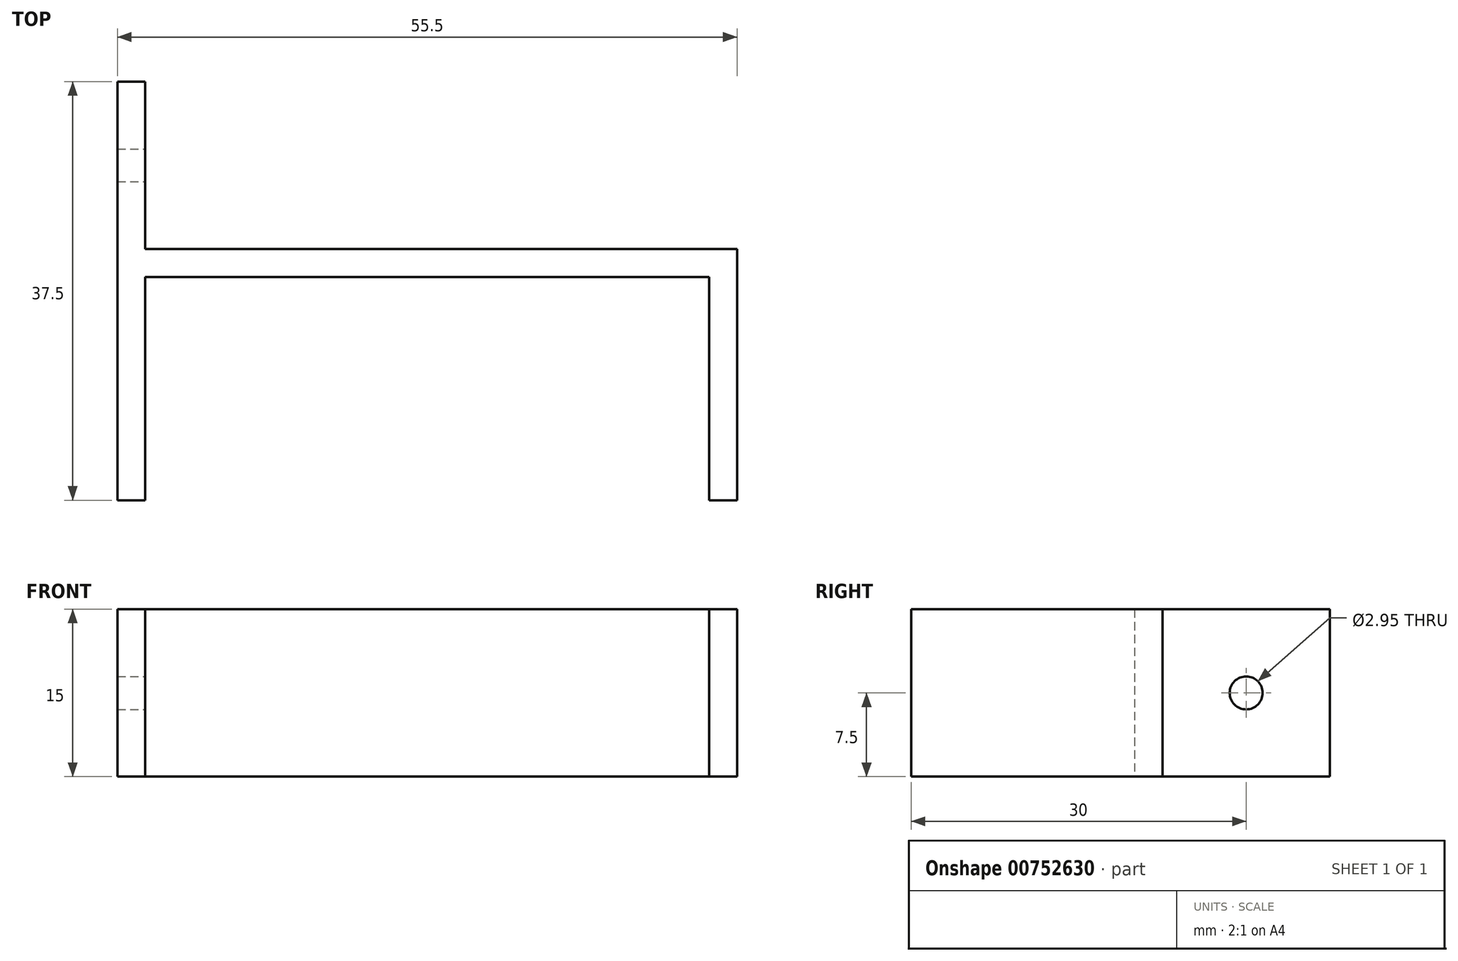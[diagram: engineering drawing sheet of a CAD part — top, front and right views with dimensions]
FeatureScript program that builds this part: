
annotation { "Feature Type Name" : "Feature", "Feature Type Description" : "" }
export const myFeature = defineFeature(function(context is Context, id is Id, definition is map)
    precondition{}
    {
        {
            var Q0;
            Q0=qCreatedBy(makeId("Top.planeOp"),FACE);
            var sketch = newSketch(context, id + "F0", { "sketchPlane" : qUnion([Q0])});
            skLineSegment(sketch, "E0", {"start": v(0, 0) * mm, "end": v(53, 0) * mm});
            skLineSegment(sketch, "E1", {"start": v(0, 15) * mm, "end": v(0, 0) * mm});
            skLineSegment(sketch, "E2", {"start": v(53, 0) * mm, "end": v(53, -22.5) * mm});
            skLineSegment(sketch, "E3", {"start": v(0, 15) * mm, "end": v(-2.5, 15) * mm});
            skLineSegment(sketch, "E4", {"start": v(-2.5, 15) * mm, "end": v(-2.5, -22.5) * mm});
            skLineSegment(sketch, "E5", {"start": v(-2.5, -22.5) * mm, "end": v(0, -22.5) * mm});
            skLineSegment(sketch, "E6", {"start": v(0, -22.5) * mm, "end": v(0, -2.5) * mm});
            skLineSegment(sketch, "E7", {"start": v(0, -2.5) * mm, "end": v(50.5, -2.5) * mm});
            skLineSegment(sketch, "E8", {"start": v(50.5, -2.5) * mm, "end": v(50.5, -22.5) * mm});
            skLineSegment(sketch, "E9", {"start": v(50.5, -22.5) * mm, "end": v(53, -22.5) * mm});
            skSolve(sketch);
        }
        {
            var Q0;
            Q0 = qSketchRegion(id + "F0", true);
            extrude(context, id + "F1", {"entities" : qUnion([Q0]), "depth" : 15 * mm, "offsetDistance" : 25 * mm});
        }
        {
            var Q0;
            Q0=makeQuery(id+"F1.opExtrude","SWEPT_FACE",FACE,{"disambiguationData":[OSD([sQuery(id+"F0.wireOp",EDGE,"E1")])]});
            var sketch = newSketch(context, id + "F2", { "sketchPlane" : qUnion([Q0])});
            skLineSegment(sketch, "E10.0", {"start": v(15, 15) * mm, "end": v(15, 0) * mm, "construction": true});
            skLineSegment(sketch, "E10.1", {"start": v(0, 15) * mm, "end": v(0, 0) * mm, "construction": true});
            skLineSegment(sketch, "E10.2", {"start": v(15, 0) * mm, "end": v(0, 0) * mm, "construction": true});
            skLineSegment(sketch, "E10.3", {"start": v(15, 15) * mm, "end": v(0, 15) * mm, "construction": true});
            skLineSegment(sketch, "E11", {"start": v(15, 0) * mm, "end": v(0, 15) * mm, "construction": true});
            skCircle(sketch, "E12", {"center": v(7.5, 7.5) * mm, "radius": 1.48 * mm});
            skSolve(sketch);
        }
        {
            var Q0;
            Q0=sQuery(id+"F2.wireOp",VERTEX,"E12.center");
            var Q1;
            Q1=makeQuery(id+"F1.opExtrude","SWEPT_BODY",BODY,{"disambiguationData":[OSD([sQuery(id+"F0.wireOp",EDGE,"E0"),sQuery(id+"F0.wireOp",EDGE,"E1"),sQuery(id+"F0.wireOp",EDGE,"E2"),sQuery(id+"F0.wireOp",EDGE,"E3"),sQuery(id+"F0.wireOp",EDGE,"E4"),sQuery(id+"F0.wireOp",EDGE,"E5"),sQuery(id+"F0.wireOp",EDGE,"E6"),sQuery(id+"F0.wireOp",EDGE,"E7"),sQuery(id+"F0.wireOp",EDGE,"E8"),sQuery(id+"F0.wireOp",EDGE,"E9")])]});
            hole(context, id + "F3", {"style" : HoleStyle.SIMPLE, "endStyle" : HoleEndStyle.THROUGH, "holeDiameter" : 2.95 * mm, "majorDiameter" : 5 * mm, "isTappedThrough" : true, "tappedDepth" : 12 * mm, "tapClearance" : 3, "locations" : qUnion([Q0]), "scope" : qUnion([Q1])});
        }
    });
